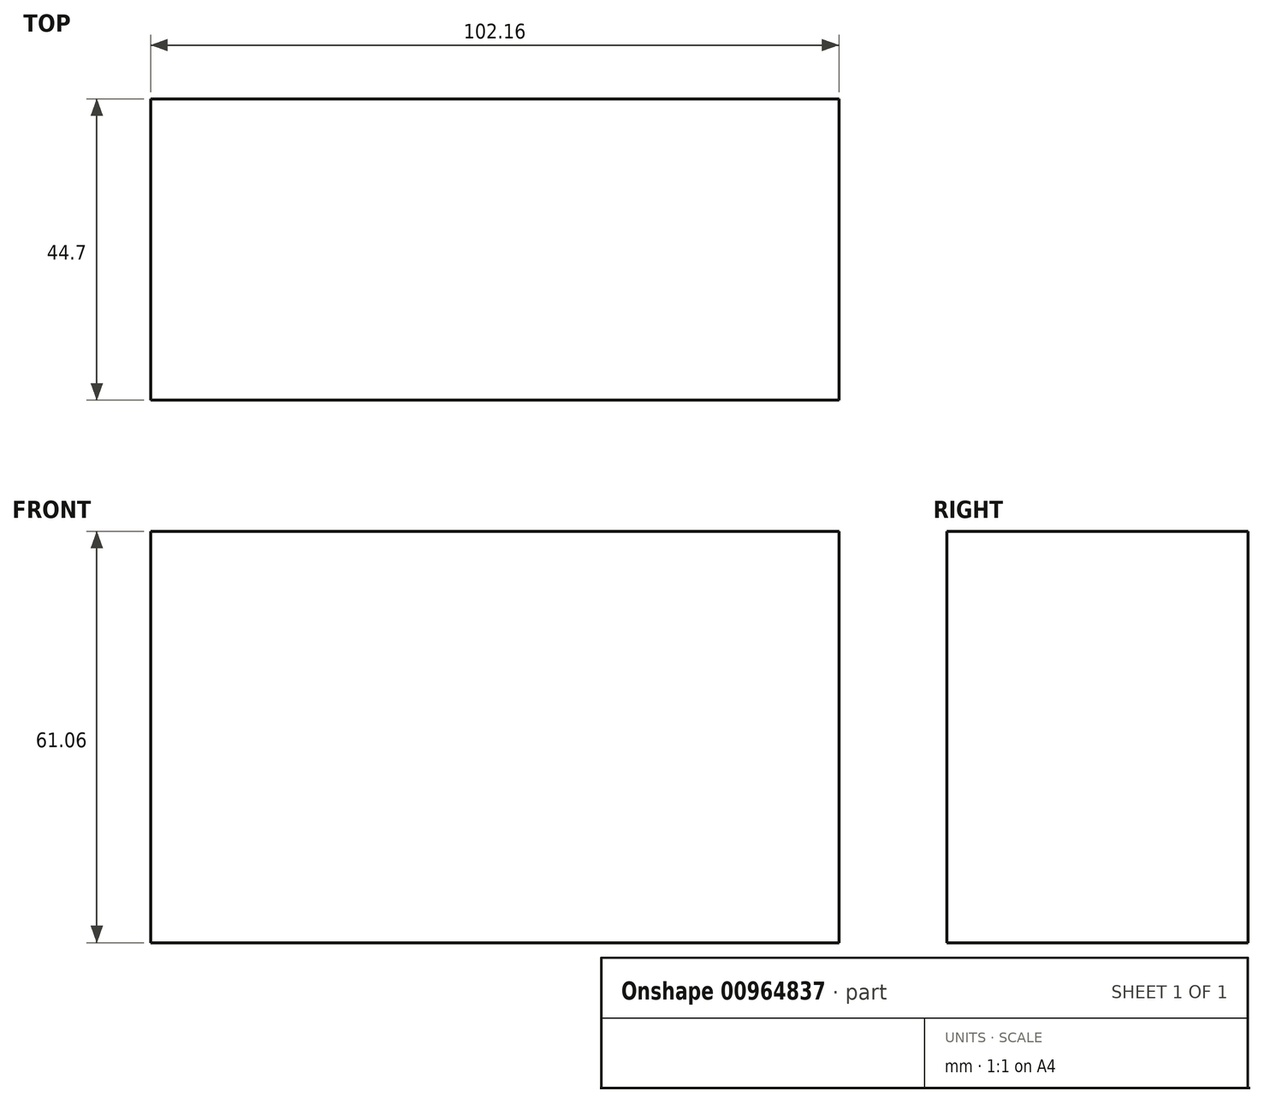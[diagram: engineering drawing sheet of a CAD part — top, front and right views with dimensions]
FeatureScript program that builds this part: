
annotation { "Feature Type Name" : "Feature", "Feature Type Description" : "" }
export const myFeature = defineFeature(function(context is Context, id is Id, definition is map)
    precondition{}
    {
        {
            var Q0;
            Q0=qCreatedBy(makeId("Front.planeOp"),FACE);
            var sketch = newSketch(context, id + "F0", { "sketchPlane" : qUnion([Q0])});
            skLineSegment(sketch, "E0.bottom", {"start": v(-48.3, 31.14) * mm, "end": v(53.87, 31.14) * mm});
            skLineSegment(sketch, "E0.top", {"start": v(-48.3, -29.92) * mm, "end": v(53.87, -29.92) * mm});
            skLineSegment(sketch, "E0.left", {"start": v(-48.3, 31.14) * mm, "end": v(-48.3, -29.92) * mm});
            skLineSegment(sketch, "E0.right", {"start": v(53.87, 31.14) * mm, "end": v(53.87, -29.92) * mm});
            skSolve(sketch);
        }
        {
            var Q0;
            Q0 = qSketchRegion(id + "F0", true);
            extrude(context, id + "F1", {"entities" : qUnion([Q0]), "depth" : 44.7 * mm, "offsetDistance" : 25.4 * mm});
        }
    });
